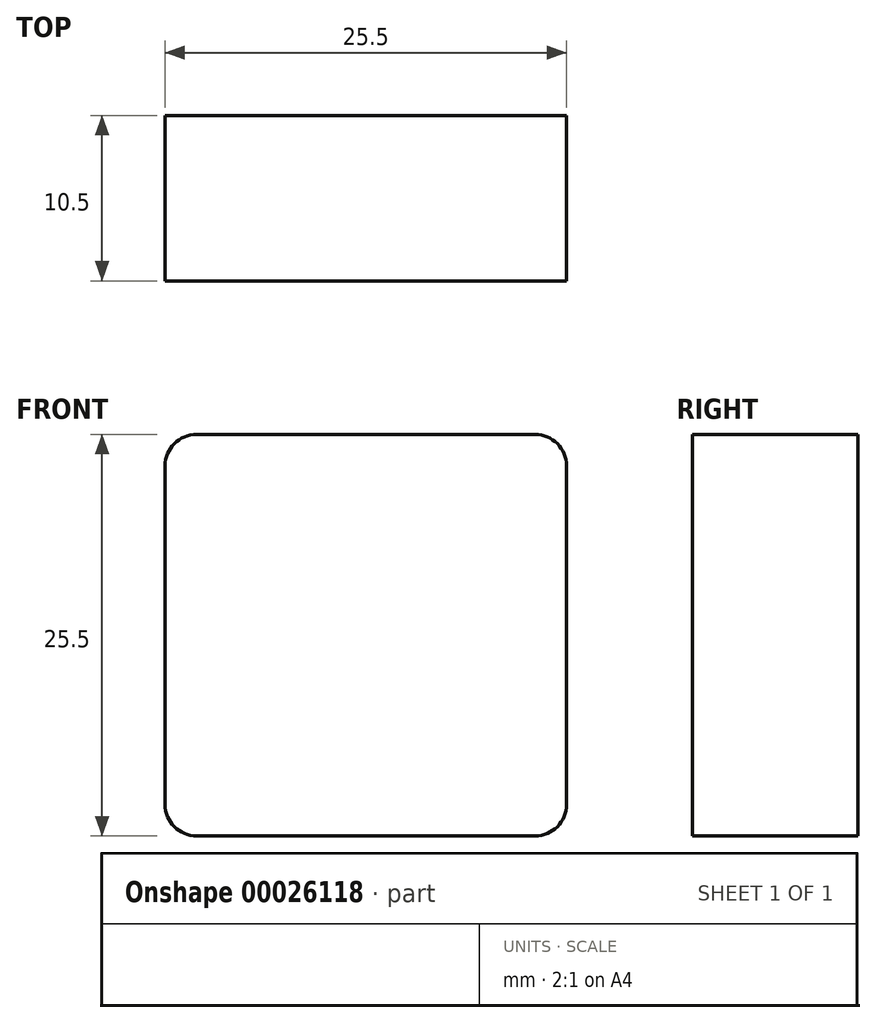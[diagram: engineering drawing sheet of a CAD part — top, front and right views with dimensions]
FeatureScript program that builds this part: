
annotation { "Feature Type Name" : "Feature", "Feature Type Description" : "" }
export const myFeature = defineFeature(function(context is Context, id is Id, definition is map)
    precondition{}
    {
        {
            var Q0;
            Q0=qCreatedBy(makeId("Front.planeOp"),FACE);
            var sketch = newSketch(context, id + "F0", { "sketchPlane" : qUnion([Q0])});
            skLineSegment(sketch, "E0.rect.bottom", {"start": v(12.75, -12.75) * mm, "end": v(-12.75, -12.75) * mm});
            skLineSegment(sketch, "E0.rect.top", {"start": v(12.75, 12.75) * mm, "end": v(-12.75, 12.75) * mm});
            skLineSegment(sketch, "E0.rect.left", {"start": v(12.75, -12.75) * mm, "end": v(12.75, 12.75) * mm});
            skLineSegment(sketch, "E0.rect.right", {"start": v(-12.75, -12.75) * mm, "end": v(-12.75, 12.75) * mm});
            skPoint(sketch, "E0.rect.middle", {"position": v(0, 0) * mm});
            skSolve(sketch);
        }
        {
            var Q0;
            Q0 = qSketchRegion(id + "F0", true);
            extrude(context, id + "F1", {"entities" : qUnion([Q0]), "depth" : 10.5 * mm});
        }
        {
            var Q0;
            Q0=makeQuery(id+"F1.opExtrude","SWEPT_EDGE",EDGE,{"disambiguationData":[OSD([sQuery(id+"F0.wireOp",EDGE,"E0.rect.top"),sQuery(id+"F0.wireOp",EDGE,"E0.rect.left")])]});
            var Q1;
            Q1=makeQuery(id+"F1.opExtrude","SWEPT_EDGE",EDGE,{"disambiguationData":[OSD([sQuery(id+"F0.wireOp",EDGE,"E0.rect.bottom"),sQuery(id+"F0.wireOp",EDGE,"E0.rect.left")])]});
            var Q2;
            Q2=makeQuery(id+"F1.opExtrude","SWEPT_EDGE",EDGE,{"disambiguationData":[OSD([sQuery(id+"F0.wireOp",EDGE,"E0.rect.top"),sQuery(id+"F0.wireOp",EDGE,"E0.rect.right")])]});
            var Q3;
            Q3=makeQuery(id+"F1.opExtrude","SWEPT_EDGE",EDGE,{"disambiguationData":[OSD([sQuery(id+"F0.wireOp",EDGE,"E0.rect.bottom"),sQuery(id+"F0.wireOp",EDGE,"E0.rect.right")])]});
            fillet(context, id + "F2", {"entities" : qUnion([Q0, Q1, Q2, Q3]), "radius" : 2 * mm, "tangentPropagation" : true, "allowEdgeOverflow" : false});
        }
    });
